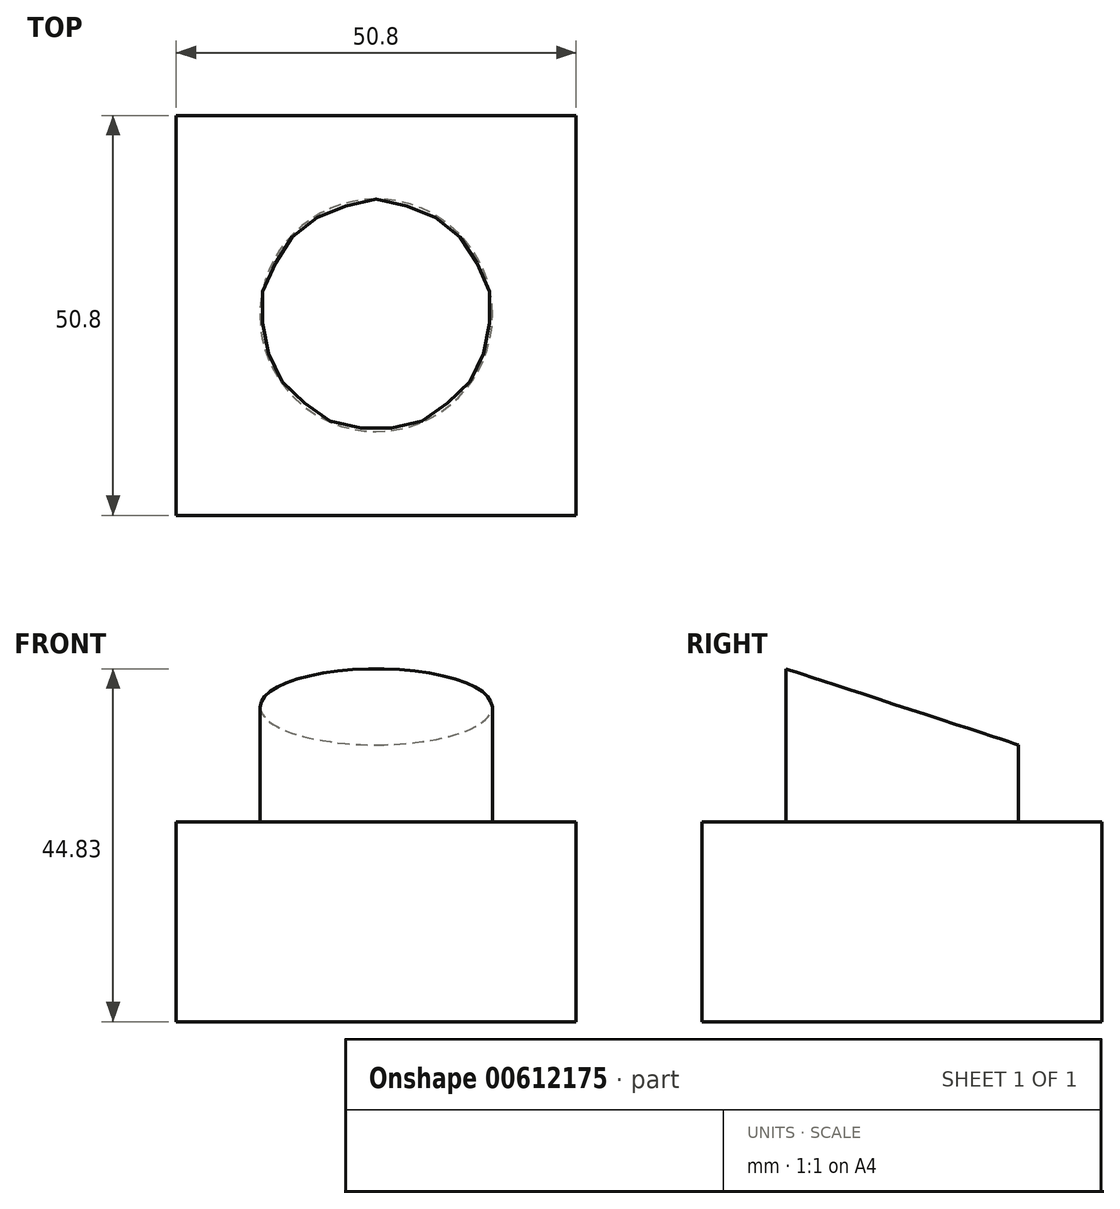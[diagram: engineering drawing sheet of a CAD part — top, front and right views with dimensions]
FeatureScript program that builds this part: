
annotation { "Feature Type Name" : "Feature", "Feature Type Description" : "" }
export const myFeature = defineFeature(function(context is Context, id is Id, definition is map)
    precondition{}
    {
        {
            var Q0;
            Q0=qCreatedBy(makeId("Top.planeOp"),FACE);
            var sketch = newSketch(context, id + "F0", { "sketchPlane" : qUnion([Q0])});
            skLineSegment(sketch, "E0.bottom", {"start": v(-25.4, 25.4) * mm, "end": v(25.4, 25.4) * mm});
            skLineSegment(sketch, "E0.top", {"start": v(-25.4, -25.4) * mm, "end": v(25.4, -25.4) * mm});
            skLineSegment(sketch, "E0.left", {"start": v(-25.4, 25.4) * mm, "end": v(-25.4, -25.4) * mm});
            skLineSegment(sketch, "E0.right", {"start": v(25.4, 25.4) * mm, "end": v(25.4, -25.4) * mm});
            skPoint(sketch, "E0.middle", {"position": v(0, 0) * mm});
            skSolve(sketch);
        }
        {
            var Q0;
            Q0 = qSketchRegion(id + "F0", true);
            extrude(context, id + "F1", {"entities" : qUnion([Q0]), "oppositeDirection" : true, "depth" : 25.4 * mm, "offsetDistance" : 25.4 * mm});
        }
        {
            var Q0;
            Q0=makeQuery(id+"F1.opExtrude","CAP_FACE",FACE,{"disambiguationData":[OSD([sQuery(id+"F0.wireOp",EDGE,"E0.bottom"),sQuery(id+"F0.wireOp",EDGE,"E0.top"),sQuery(id+"F0.wireOp",EDGE,"E0.left"),sQuery(id+"F0.wireOp",EDGE,"E0.right")])],"isStart":true});
            var sketch = newSketch(context, id + "F2", { "sketchPlane" : qUnion([Q0])});
            skCircle(sketch, "E1", {"center": v(0, 0) * mm, "radius": 14.77 * mm});
            skSolve(sketch);
        }
        {
            var Q0;
            Q0=makeQuery(id+"F2.imprint","IMPRINT",FACE,{"disambiguationData":[TD([[makeQuery(id+"F2.imprint","IMPRINT",EDGE,{"derivedFrom":sQuery(id+"F2.wireOp",EDGE,"E1")}),1.0]])]});
            extrude(context, id + "F3", {"entities" : qUnion([Q0]), "operationType" : NewBodyOperationType.ADD, "depth" : 25.4 * mm, "offsetDistance" : 25.4 * mm});
        }
        {
            var Q0;
            Q0=qCreatedBy(makeId("Right.planeOp"),FACE);
            var sketch = newSketch(context, id + "F4", { "sketchPlane" : qUnion([Q0])});
            skLineSegment(sketch, "E2", {"start": v(-20.69, 21.37) * mm, "end": v(29.32, 5) * mm});
            skLineSegment(sketch, "E3", {"start": v(29.32, 5) * mm, "end": v(29.32, 40.46) * mm});
            skLineSegment(sketch, "E4", {"start": v(29.32, 40.46) * mm, "end": v(-22.96, 40.46) * mm});
            skLineSegment(sketch, "E5", {"start": v(-22.96, 40.46) * mm, "end": v(-20.69, 21.37) * mm});
            skSolve(sketch);
        }
        {
            var Q0;
            Q0=makeQuery(id+"F4.imprint","IMPRINT",FACE,{"disambiguationData":[TD([[makeQuery(id+"F4.imprint","IMPRINT",EDGE,{"derivedFrom":sQuery(id+"F4.wireOp",EDGE,"E2")}),1.0]])]});
            extrude(context, id + "F5", {"entities" : qUnion([Q0]), "operationType" : NewBodyOperationType.REMOVE, "oppositeDirection" : true, "depth" : 50.8 * mm, "offsetDistance" : 25.4 * mm, "symmetric" : true});
        }
    });
